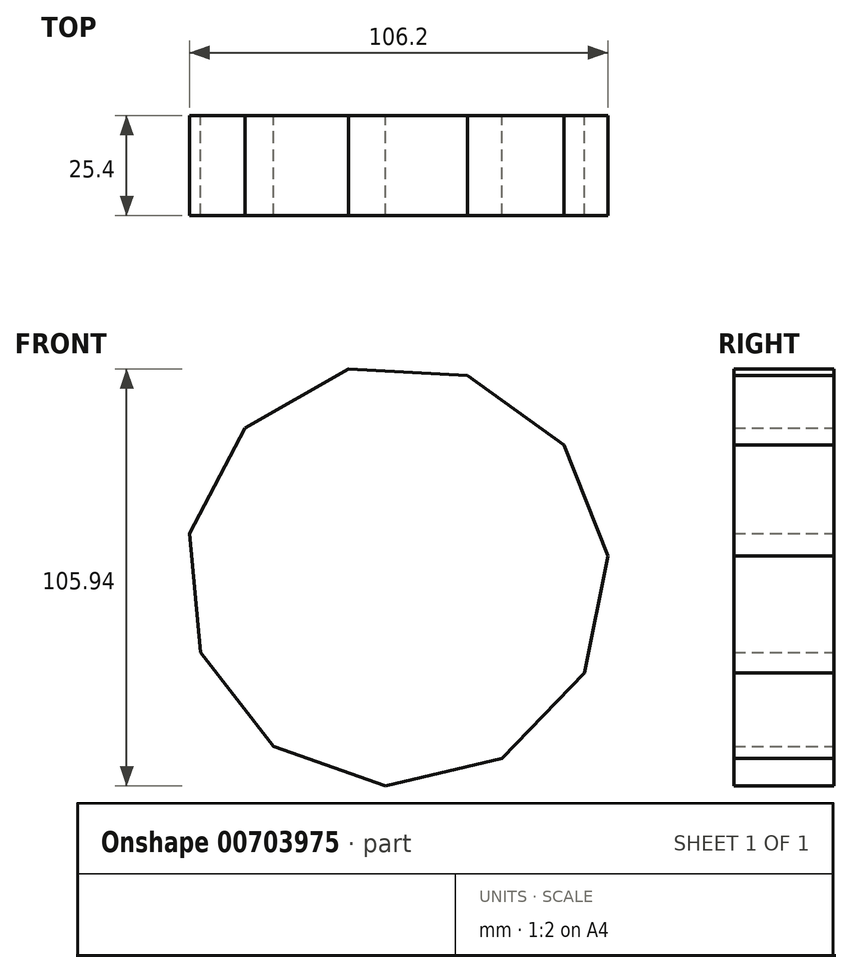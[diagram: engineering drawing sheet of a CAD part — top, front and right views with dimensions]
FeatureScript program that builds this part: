
annotation { "Feature Type Name" : "Feature", "Feature Type Description" : "" }
export const myFeature = defineFeature(function(context is Context, id is Id, definition is map)
    precondition{}
    {
        {
            var Q0;
            Q0=qCreatedBy(makeId("Front.planeOp"),FACE);
            var sketch = newSketch(context, id + "F0", { "sketchPlane" : qUnion([Q0])});
            skCircle(sketch, "E0.cCircle", {"center": v(0, 0) * mm, "radius": 51.55 * mm, "construction": true});
            skLineSegment(sketch, "E0.0", {"start": v(-38.65, 37.31) * mm, "end": v(-12.34, 52.29) * mm});
            skLineSegment(sketch, "E0.1", {"start": v(-12.34, 52.29) * mm, "end": v(17.88, 50.66) * mm});
            skLineSegment(sketch, "E0.2", {"start": v(17.88, 50.66) * mm, "end": v(42.43, 32.95) * mm});
            skLineSegment(sketch, "E0.3", {"start": v(42.43, 32.95) * mm, "end": v(53.51, 4.78) * mm});
            skLineSegment(sketch, "E0.4", {"start": v(53.51, 4.78) * mm, "end": v(47.6, -24.91) * mm});
            skLineSegment(sketch, "E0.5", {"start": v(47.6, -24.91) * mm, "end": v(26.58, -46.7) * mm});
            skLineSegment(sketch, "E0.6", {"start": v(26.58, -46.7) * mm, "end": v(-2.89, -53.65) * mm});
            skLineSegment(sketch, "E0.7", {"start": v(-2.89, -53.65) * mm, "end": v(-31.43, -43.57) * mm});
            skLineSegment(sketch, "E0.8", {"start": v(-31.43, -43.57) * mm, "end": v(-50, -19.66) * mm});
            skLineSegment(sketch, "E0.9", {"start": v(-50, -19.66) * mm, "end": v(-52.7, 10.5) * mm});
            skLineSegment(sketch, "E0.10", {"start": v(-52.7, 10.5) * mm, "end": v(-38.65, 37.31) * mm});
            skPoint(sketch, "E0.0.midPoint", {"position": v(-25.5, 44.8) * mm});
            skSolve(sketch);
        }
        {
            var Q0;
            Q0 = qSketchRegion(id + "F0", true);
            extrude(context, id + "F1", {"entities" : qUnion([Q0]), "depth" : 25.4 * mm, "offsetDistance" : 25.4 * mm});
        }
    });
